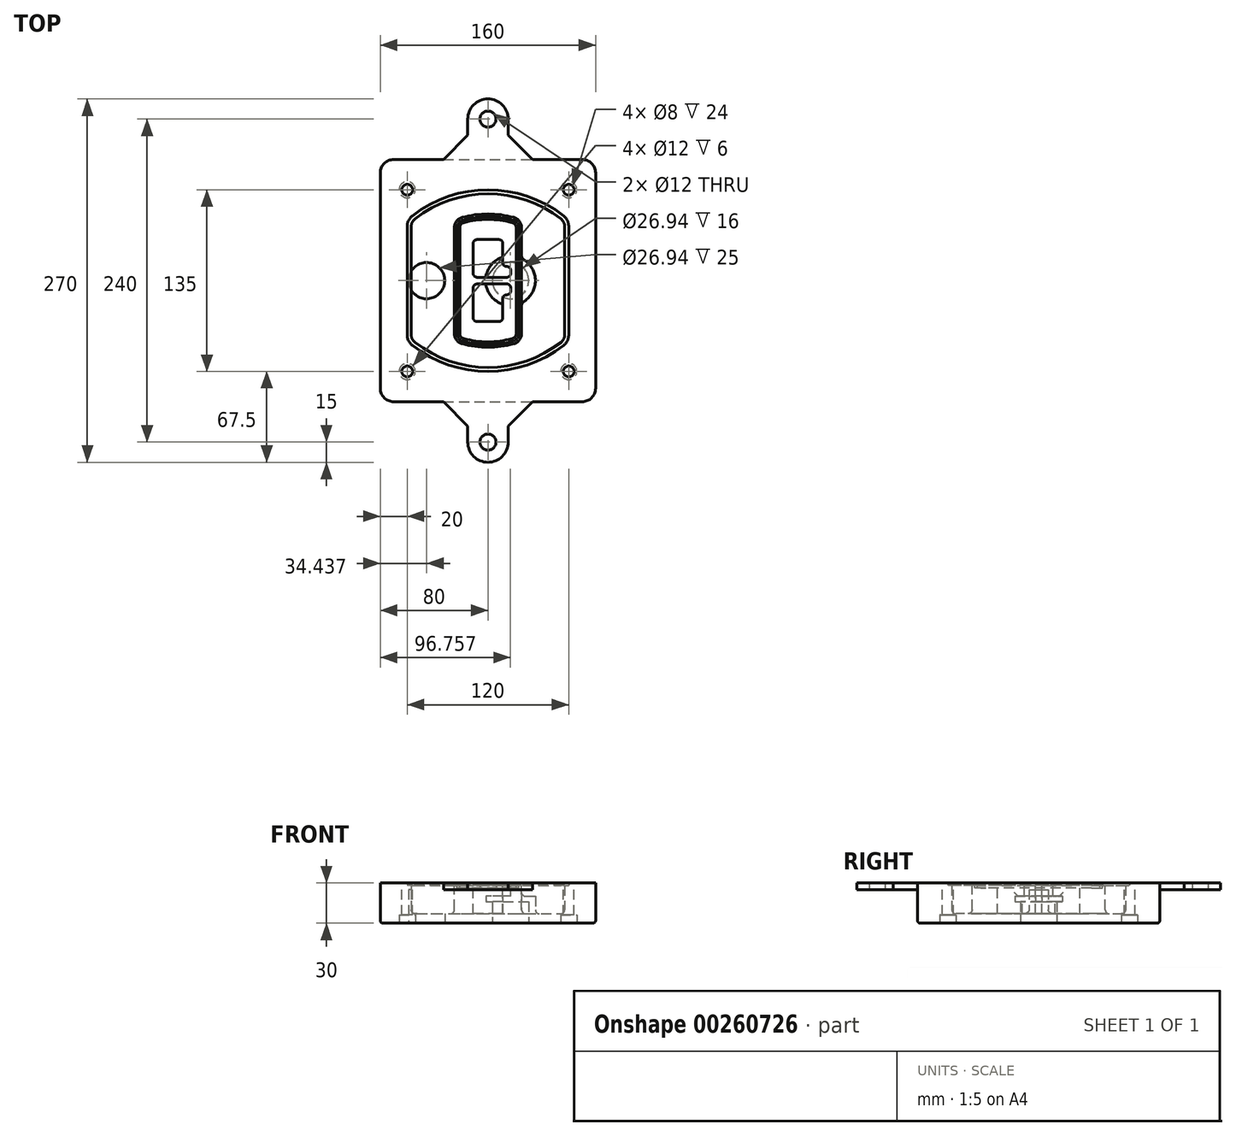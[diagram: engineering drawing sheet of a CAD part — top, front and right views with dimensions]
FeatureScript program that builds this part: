
annotation { "Feature Type Name" : "Feature", "Feature Type Description" : "" }
export const myFeature = defineFeature(function(context is Context, id is Id, definition is map)
    precondition{}
    {
        {
            var Q0;
            Q0=qCreatedBy(makeId("Top.planeOp"),FACE);
            var sketch = newSketch(context, id + "F0", { "sketchPlane" : qUnion([Q0])});
            skPoint(sketch, "E0.rect.middle", {"position": v(0, 0) * mm});
            skLineSegment(sketch, "E1.bottom", {"start": v(-70, -90) * mm, "end": v(70, -90) * mm});
            skLineSegment(sketch, "E1.top", {"start": v(-70, 90) * mm, "end": v(70, 90) * mm});
            skLineSegment(sketch, "E1.left", {"start": v(-80, -80) * mm, "end": v(-80, 80) * mm});
            skLineSegment(sketch, "E1.right", {"start": v(80, -80) * mm, "end": v(80, 80) * mm});
            skLineSegment(sketch, "E2", {"start": v(-80, 90) * mm, "end": v(80, -90) * mm, "construction": true});
            skLineSegment(sketch, "E3", {"start": v(80, 90) * mm, "end": v(-80, -90) * mm, "construction": true});
            skCircle(sketch, "E4", {"center": v(-60, 67.5) * mm, "radius": 4 * mm});
            skCircle(sketch, "E5", {"center": v(60, 67.5) * mm, "radius": 4 * mm});
            skCircle(sketch, "E6", {"center": v(60, -67.5) * mm, "radius": 4 * mm});
            skCircle(sketch, "E7", {"center": v(-60, -67.5) * mm, "radius": 4 * mm});
            skLineSegment(sketch, "E8", {"start": v(-60, 67.5) * mm, "end": v(60, 67.5) * mm, "construction": true});
            skLineSegment(sketch, "E9", {"start": v(60, 67.5) * mm, "end": v(60, -67.5) * mm, "construction": true});
            skLineSegment(sketch, "E10", {"start": v(60, -67.5) * mm, "end": v(-60, -67.5) * mm, "construction": true});
            skLineSegment(sketch, "E11", {"start": v(-60, -67.5) * mm, "end": v(-60, 67.5) * mm, "construction": true});
            skLineSegment(sketch, "E12", {"start": v(-60, 40.3) * mm, "end": v(-60, -40.3) * mm});
            skLineSegment(sketch, "E13", {"start": v(60, 40.3) * mm, "end": v(60, -40.3) * mm});
            skArc(sketch, "E14", {"start": v(56.15, 48.18) * mm, "mid": v(0, 67.5) * mm, "end": v(-56.15, 48.18) * mm});
            skArc(sketch, "E15", {"start": v(-56.15, -48.18) * mm, "mid": v(0, -67.5) * mm, "end": v(56.15, -48.18) * mm});
            skLineSegment(sketch, "E16", {"start": v(-60, 0) * mm, "end": v(60, 0) * mm, "construction": true});
            skPoint(sketch, "E17.visualSharp", {"position": v(-60, -45) * mm});
            skArc(sketch, "E17.filletArc", {"start": v(-60, -40.3) * mm, "mid": v(-58.99, -44.68) * mm, "end": v(-56.15, -48.18) * mm});
            skPoint(sketch, "E18.visualSharp", {"position": v(-60, 45) * mm});
            skArc(sketch, "E18.filletArc", {"start": v(-56.15, 48.18) * mm, "mid": v(-58.99, 44.68) * mm, "end": v(-60, 40.3) * mm});
            skPoint(sketch, "E19.visualSharp", {"position": v(60, 45) * mm});
            skArc(sketch, "E19.filletArc", {"start": v(60, 40.3) * mm, "mid": v(58.99, 44.68) * mm, "end": v(56.15, 48.18) * mm});
            skPoint(sketch, "E20.visualSharp", {"position": v(60, -45) * mm});
            skArc(sketch, "E20.filletArc", {"start": v(56.15, -48.18) * mm, "mid": v(58.99, -44.68) * mm, "end": v(60, -40.3) * mm});
            skPoint(sketch, "E21.visualSharp", {"position": v(-80, 90) * mm});
            skArc(sketch, "E21.filletArc", {"start": v(-70, 90) * mm, "mid": v(-77.07, 87.07) * mm, "end": v(-80, 80) * mm});
            skPoint(sketch, "E22.visualSharp", {"position": v(80, 90) * mm});
            skArc(sketch, "E22.filletArc", {"start": v(80, 80) * mm, "mid": v(77.07, 87.07) * mm, "end": v(70, 90) * mm});
            skPoint(sketch, "E23.visualSharp", {"position": v(80, -90) * mm});
            skArc(sketch, "E23.filletArc", {"start": v(70, -90) * mm, "mid": v(77.07, -87.07) * mm, "end": v(80, -80) * mm});
            skPoint(sketch, "E24.visualSharp", {"position": v(-80, -90) * mm});
            skArc(sketch, "E24.filletArc", {"start": v(-80, -80) * mm, "mid": v(-77.07, -87.07) * mm, "end": v(-70, -90) * mm});
            skArc(sketch, "E25.0", {"start": v(57, 40.3) * mm, "mid": v(56.3, 43.36) * mm, "end": v(54.3, 45.81) * mm});
            skLineSegment(sketch, "E25.1", {"start": v(57, 40.3) * mm, "end": v(57, -40.3) * mm});
            skArc(sketch, "E25.2", {"start": v(54.3, -45.81) * mm, "mid": v(56.3, -43.36) * mm, "end": v(57, -40.3) * mm});
            skArc(sketch, "E25.3", {"start": v(-54.3, -45.81) * mm, "mid": v(0, -64.5) * mm, "end": v(54.3, -45.81) * mm});
            skArc(sketch, "E25.4", {"start": v(-57, -40.3) * mm, "mid": v(-56.3, -43.36) * mm, "end": v(-54.3, -45.81) * mm});
            skArc(sketch, "E25.5", {"start": v(54.3, 45.81) * mm, "mid": v(0, 64.5) * mm, "end": v(-54.3, 45.81) * mm});
            skLineSegment(sketch, "E25.6", {"start": v(-57, 40.3) * mm, "end": v(-57, -40.3) * mm});
            skArc(sketch, "E25.7", {"start": v(-54.3, 45.81) * mm, "mid": v(-56.3, 43.36) * mm, "end": v(-57, 40.3) * mm});
            skArc(sketch, "E26.0", {"start": v(-58.62, 51.33) * mm, "mid": v(-62.58, 46.43) * mm, "end": v(-64, 40.3) * mm});
            skArc(sketch, "E26.1", {"start": v(58.62, 51.33) * mm, "mid": v(0, 71.5) * mm, "end": v(-58.62, 51.33) * mm});
            skArc(sketch, "E26.2", {"start": v(64, 40.3) * mm, "mid": v(62.58, 46.43) * mm, "end": v(58.62, 51.33) * mm});
            skLineSegment(sketch, "E26.3", {"start": v(64, 40.3) * mm, "end": v(64, -40.3) * mm});
            skArc(sketch, "E26.4", {"start": v(58.62, -51.33) * mm, "mid": v(62.58, -46.43) * mm, "end": v(64, -40.3) * mm});
            skLineSegment(sketch, "E26.5", {"start": v(-64, 40.3) * mm, "end": v(-64, -40.3) * mm});
            skArc(sketch, "E26.6", {"start": v(-58.62, -51.33) * mm, "mid": v(0, -71.5) * mm, "end": v(58.62, -51.33) * mm});
            skArc(sketch, "E26.7", {"start": v(-64, -40.3) * mm, "mid": v(-62.58, -46.43) * mm, "end": v(-58.62, -51.33) * mm});
            skSolve(sketch);
        }
        {
            var Q0;
            Q0=makeQuery(id+"F0.imprint","IMPRINT",FACE,{"disambiguationData":[TD([[makeQuery(id+"F0.imprint","IMPRINT",EDGE,{"derivedFrom":sQuery(id+"F0.wireOp",EDGE,"E1.bottom")}),1.0]])]});
            var Q1;
            Q1=makeQuery(id+"F0.imprint","IMPRINT",FACE,{"disambiguationData":[TD([[makeQuery(id+"F0.imprint","IMPRINT",EDGE,{"derivedFrom":sQuery(id+"F0.wireOp",EDGE,"E12")}),1.0]])]});
            var Q2;
            Q2=makeQuery(id+"F0.imprint","IMPRINT",FACE,{"disambiguationData":[TD([[makeQuery(id+"F0.imprint","IMPRINT",EDGE,{"derivedFrom":sQuery(id+"F0.wireOp",EDGE,"E25.0")}),1.0]])]});
            var Q3;
            Q3=makeQuery(id+"F0.imprint","IMPRINT",FACE,{"disambiguationData":[TD([[makeQuery(id+"F0.imprint","IMPRINT",EDGE,{"derivedFrom":sQuery(id+"F0.wireOp",EDGE,"E12")}),-1.0]])]});
            extrude(context, id + "F1", {"entities" : qUnion([Q0, Q1, Q2, Q3]), "oppositeDirection" : true, "depth" : 25 * mm});
        }
        {
            var Q0;
            Q0=makeQuery(id+"F0.imprint","IMPRINT",FACE,{"disambiguationData":[TD([[makeQuery(id+"F0.imprint","IMPRINT",EDGE,{"derivedFrom":sQuery(id+"F0.wireOp",EDGE,"E12")}),1.0]])]});
            extrude(context, id + "F2", {"entities" : qUnion([Q0]), "operationType" : NewBodyOperationType.ADD, "depth" : 3 * mm});
        }
        {
            var Q0;
            Q0=makeQuery(id+"F0.imprint","IMPRINT",FACE,{"disambiguationData":[TD([[makeQuery(id+"F0.imprint","IMPRINT",EDGE,{"derivedFrom":sQuery(id+"F0.wireOp",EDGE,"E25.0")}),1.0]])]});
            extrude(context, id + "F3", {"entities" : qUnion([Q0]), "operationType" : NewBodyOperationType.REMOVE, "oppositeDirection" : true, "depth" : 18 * mm});
        }
        {
            var Q0;
            Q0=makeQuery(id+"F2.opExtrude","CAP_FACE",FACE,{"disambiguationData":[OSD([sQuery(id+"F0.wireOp",EDGE,"E12"),sQuery(id+"F0.wireOp",EDGE,"E13"),sQuery(id+"F0.wireOp",EDGE,"E14"),sQuery(id+"F0.wireOp",EDGE,"E15"),sQuery(id+"F0.wireOp",EDGE,"E17.filletArc"),sQuery(id+"F0.wireOp",EDGE,"E18.filletArc"),sQuery(id+"F0.wireOp",EDGE,"E19.filletArc"),sQuery(id+"F0.wireOp",EDGE,"E20.filletArc"),sQuery(id+"F0.wireOp",EDGE,"E25.0"),sQuery(id+"F0.wireOp",EDGE,"E25.1"),sQuery(id+"F0.wireOp",EDGE,"E25.2"),sQuery(id+"F0.wireOp",EDGE,"E25.3"),sQuery(id+"F0.wireOp",EDGE,"E25.4"),sQuery(id+"F0.wireOp",EDGE,"E25.5"),sQuery(id+"F0.wireOp",EDGE,"E25.6"),sQuery(id+"F0.wireOp",EDGE,"E25.7")])],"isStart":false});
            var sketch = newSketch(context, id + "F4", { "sketchPlane" : qUnion([Q0])});
            skArc(sketch, "E27.0", {"start": v(-19.08, -46.97) * mm, "mid": v(0, -49.5) * mm, "end": v(19.08, -46.97) * mm});
            skArc(sketch, "E28.0", {"start": v(19.08, 46.97) * mm, "mid": v(0, 49.5) * mm, "end": v(-19.08, 46.97) * mm});
            skLineSegment(sketch, "E29", {"start": v(-25, 39.25) * mm, "end": v(-25, -39.25) * mm});
            skLineSegment(sketch, "E30", {"start": v(25, 39.25) * mm, "end": v(25, -39.25) * mm});
            skLineSegment(sketch, "E31", {"start": v(-25, 45.1) * mm, "end": v(25, 45.1) * mm, "construction": true});
            skLineSegment(sketch, "E32", {"start": v(-25, -45.1) * mm, "end": v(25, -45.1) * mm, "construction": true});
            skPoint(sketch, "E33.visualSharp", {"position": v(-25, 45.1) * mm});
            skArc(sketch, "E33.filletArc", {"start": v(-19.08, 46.97) * mm, "mid": v(-23.35, 44.11) * mm, "end": v(-25, 39.25) * mm});
            skPoint(sketch, "E34.visualSharp", {"position": v(25, 45.1) * mm});
            skArc(sketch, "E34.filletArc", {"start": v(25, 39.25) * mm, "mid": v(23.35, 44.11) * mm, "end": v(19.08, 46.97) * mm});
            skPoint(sketch, "E35.visualSharp", {"position": v(25, -45.1) * mm});
            skArc(sketch, "E35.filletArc", {"start": v(19.08, -46.97) * mm, "mid": v(23.35, -44.11) * mm, "end": v(25, -39.25) * mm});
            skPoint(sketch, "E36.visualSharp", {"position": v(-25, -45.1) * mm});
            skArc(sketch, "E36.filletArc", {"start": v(-25, -39.25) * mm, "mid": v(-23.35, -44.11) * mm, "end": v(-19.08, -46.97) * mm});
            skArc(sketch, "E37.0", {"start": v(54.3, 45.81) * mm, "mid": v(0, 64.5) * mm, "end": v(-54.3, 45.81) * mm});
            skArc(sketch, "E37.1", {"start": v(-54.3, 45.81) * mm, "mid": v(-56.3, 43.36) * mm, "end": v(-57, 40.3) * mm});
            skLineSegment(sketch, "E37.2", {"start": v(-57, 40.3) * mm, "end": v(-57, -40.3) * mm});
            skArc(sketch, "E37.3", {"start": v(-57, -40.3) * mm, "mid": v(-56.3, -43.36) * mm, "end": v(-54.3, -45.81) * mm});
            skArc(sketch, "E37.4", {"start": v(-54.3, -45.81) * mm, "mid": v(0, -64.5) * mm, "end": v(54.3, -45.81) * mm});
            skArc(sketch, "E37.5", {"start": v(54.3, -45.81) * mm, "mid": v(56.3, -43.36) * mm, "end": v(57, -40.3) * mm});
            skLineSegment(sketch, "E37.6", {"start": v(57, 40.3) * mm, "end": v(57, -40.3) * mm});
            skArc(sketch, "E37.7", {"start": v(57, 40.3) * mm, "mid": v(56.3, 43.36) * mm, "end": v(54.3, 45.81) * mm});
            skLineSegment(sketch, "E38.0", {"start": v(23, 39.25) * mm, "end": v(23, -39.25) * mm});
            skArc(sketch, "E38.1", {"start": v(18.56, -45.04) * mm, "mid": v(21.76, -42.9) * mm, "end": v(23, -39.25) * mm});
            skArc(sketch, "E38.2", {"start": v(-18.56, -45.04) * mm, "mid": v(0, -47.5) * mm, "end": v(18.56, -45.04) * mm});
            skArc(sketch, "E38.3", {"start": v(-23, -39.25) * mm, "mid": v(-21.76, -42.9) * mm, "end": v(-18.56, -45.04) * mm});
            skLineSegment(sketch, "E38.4", {"start": v(-23, 39.25) * mm, "end": v(-23, -39.25) * mm});
            skArc(sketch, "E38.5", {"start": v(23, 39.25) * mm, "mid": v(21.76, 42.9) * mm, "end": v(18.56, 45.04) * mm});
            skArc(sketch, "E38.6", {"start": v(-18.56, 45.04) * mm, "mid": v(-21.76, 42.9) * mm, "end": v(-23, 39.25) * mm});
            skArc(sketch, "E38.7", {"start": v(18.56, 45.04) * mm, "mid": v(0, 47.5) * mm, "end": v(-18.56, 45.04) * mm});
            skArc(sketch, "E39.0", {"start": v(21, 39.25) * mm, "mid": v(20.18, 41.68) * mm, "end": v(18.04, 43.1) * mm});
            skLineSegment(sketch, "E39.1", {"start": v(21, 39.25) * mm, "end": v(21, -39.25) * mm});
            skArc(sketch, "E39.2", {"start": v(18.04, -43.1) * mm, "mid": v(20.18, -41.68) * mm, "end": v(21, -39.25) * mm});
            skArc(sketch, "E39.3", {"start": v(-18.04, -43.1) * mm, "mid": v(0, -45.5) * mm, "end": v(18.04, -43.1) * mm});
            skArc(sketch, "E39.4", {"start": v(-21, -39.25) * mm, "mid": v(-20.18, -41.68) * mm, "end": v(-18.04, -43.1) * mm});
            skArc(sketch, "E39.5", {"start": v(18.04, 43.1) * mm, "mid": v(0, 45.5) * mm, "end": v(-18.04, 43.1) * mm});
            skLineSegment(sketch, "E39.6", {"start": v(-21, 39.25) * mm, "end": v(-21, -39.25) * mm});
            skArc(sketch, "E39.7", {"start": v(-18.04, 43.1) * mm, "mid": v(-20.18, 41.68) * mm, "end": v(-21, 39.25) * mm});
            skLineSegment(sketch, "E40", {"start": v(-25, 0) * mm, "end": v(25, 0) * mm, "construction": true});
            skLineSegment(sketch, "E41", {"start": v(-11, 5.5) * mm, "end": v(-11, 27.5) * mm});
            skLineSegment(sketch, "E42", {"start": v(-8, 30.5) * mm, "end": v(8, 30.5) * mm});
            skLineSegment(sketch, "E43", {"start": v(11, 27.5) * mm, "end": v(11, 13.5) * mm});
            skLineSegment(sketch, "E44", {"start": v(14, 10.5) * mm, "end": v(14, 10.5) * mm});
            skLineSegment(sketch, "E45", {"start": v(17, 7.5) * mm, "end": v(17, 5.5) * mm});
            skLineSegment(sketch, "E46", {"start": v(14, 2.5) * mm, "end": v(-8, 2.5) * mm});
            skPoint(sketch, "E47.visualSharp", {"position": v(-11, 30.5) * mm});
            skArc(sketch, "E47.filletArc", {"start": v(-8, 30.5) * mm, "mid": v(-10.12, 29.62) * mm, "end": v(-11, 27.5) * mm});
            skPoint(sketch, "E48.visualSharp", {"position": v(11, 30.5) * mm});
            skArc(sketch, "E48.filletArc", {"start": v(11, 27.5) * mm, "mid": v(10.12, 29.62) * mm, "end": v(8, 30.5) * mm});
            skPoint(sketch, "E49.visualSharp", {"position": v(11, 10.5) * mm});
            skArc(sketch, "E49.filletArc", {"start": v(11, 13.5) * mm, "mid": v(11.88, 11.38) * mm, "end": v(14, 10.5) * mm});
            skPoint(sketch, "E50.visualSharp", {"position": v(17, 10.5) * mm});
            skArc(sketch, "E50.filletArc", {"start": v(17, 7.5) * mm, "mid": v(16.12, 9.62) * mm, "end": v(14, 10.5) * mm});
            skPoint(sketch, "E51.visualSharp", {"position": v(17, 2.5) * mm});
            skArc(sketch, "E51.filletArc", {"start": v(14, 2.5) * mm, "mid": v(16.12, 3.38) * mm, "end": v(17, 5.5) * mm});
            skPoint(sketch, "E52.visualSharp", {"position": v(-11, 2.5) * mm});
            skArc(sketch, "E52.filletArc", {"start": v(-11, 5.5) * mm, "mid": v(-10.12, 3.38) * mm, "end": v(-8, 2.5) * mm});
            skLineSegment(sketch, "E53.0.MirrorCS", {"start": v(14, -2.5) * mm, "end": v(-8, -2.5) * mm});
            skArc(sketch, "E54.0.MirrorCS", {"start": v(-11, -5.5) * mm, "mid": v(-10.12, -3.38) * mm, "end": v(-8, -2.5) * mm});
            skLineSegment(sketch, "E55.0.MirrorCS", {"start": v(-11, -5.5) * mm, "end": v(-11, -27.5) * mm});
            skArc(sketch, "E56.0.MirrorCS", {"start": v(-8, -30.5) * mm, "mid": v(-10.12, -29.62) * mm, "end": v(-11, -27.5) * mm});
            skLineSegment(sketch, "E57.0.MirrorCS", {"start": v(-8, -30.5) * mm, "end": v(8, -30.5) * mm});
            skArc(sketch, "E58.0.MirrorCS", {"start": v(11, -27.5) * mm, "mid": v(10.12, -29.62) * mm, "end": v(8, -30.5) * mm});
            skLineSegment(sketch, "E59.0.MirrorCS", {"start": v(11, -27.5) * mm, "end": v(11, -13.5) * mm});
            skArc(sketch, "E60.0.MirrorCS", {"start": v(11, -13.5) * mm, "mid": v(11.88, -11.38) * mm, "end": v(14, -10.5) * mm});
            skArc(sketch, "E61.0.MirrorCS", {"start": v(17, -7.5) * mm, "mid": v(16.12, -9.62) * mm, "end": v(14, -10.5) * mm});
            skLineSegment(sketch, "E62.0.MirrorCS", {"start": v(17, -7.5) * mm, "end": v(17, -5.5) * mm});
            skArc(sketch, "E63.0.MirrorCS", {"start": v(14, -2.5) * mm, "mid": v(16.12, -3.38) * mm, "end": v(17, -5.5) * mm});
            skSolve(sketch);
        }
        {
            var Q0;
            Q0=makeQuery(id+"F4.imprint","IMPRINT",FACE,{"disambiguationData":[TD([[makeQuery(id+"F4.imprint","IMPRINT",EDGE,{"derivedFrom":sQuery(id+"F4.wireOp",EDGE,"E27.0")}),1.0]])]});
            var Q1;
            Q1=makeQuery(id+"F4.imprint","IMPRINT",FACE,{"disambiguationData":[TD([[makeQuery(id+"F4.imprint","IMPRINT",EDGE,{"derivedFrom":sQuery(id+"F4.wireOp",EDGE,"E38.0")}),-1.0]])]});
            var Q2;
            Q2=makeQuery(id+"F4.imprint","IMPRINT",FACE,{"disambiguationData":[TD([[makeQuery(id+"F4.imprint","IMPRINT",EDGE,{"derivedFrom":sQuery(id+"F4.wireOp",EDGE,"E39.0")}),1.0]])]});
            extrude(context, id + "F5", {"entities" : qUnion([Q0, Q1, Q2]), "operationType" : NewBodyOperationType.ADD, "endBound" : BoundingType.UP_TO_NEXT, "oppositeDirection" : true, "depth" : 25 * mm});
        }
        {
            var Q0;
            Q0=makeQuery(id+"F4.imprint","IMPRINT",FACE,{"disambiguationData":[TD([[makeQuery(id+"F4.imprint","IMPRINT",EDGE,{"derivedFrom":sQuery(id+"F4.wireOp",EDGE,"E38.0")}),-1.0]])]});
            extrude(context, id + "F6", {"entities" : qUnion([Q0]), "operationType" : NewBodyOperationType.REMOVE, "oppositeDirection" : true, "depth" : 2 * mm});
        }
        {
            var Q0;
            Q0=makeQuery(id+"F1.opExtrude","CAP_FACE",FACE,{"disambiguationData":[OSD([sQuery(id+"F0.wireOp",EDGE,"E1.bottom"),sQuery(id+"F0.wireOp",EDGE,"E1.top"),sQuery(id+"F0.wireOp",EDGE,"E1.left"),sQuery(id+"F0.wireOp",EDGE,"E1.right"),sQuery(id+"F0.wireOp",EDGE,"E4"),sQuery(id+"F0.wireOp",EDGE,"E5"),sQuery(id+"F0.wireOp",EDGE,"E6"),sQuery(id+"F0.wireOp",EDGE,"E7"),sQuery(id+"F0.wireOp",EDGE,"E21.filletArc"),sQuery(id+"F0.wireOp",EDGE,"E22.filletArc"),sQuery(id+"F0.wireOp",EDGE,"E23.filletArc"),sQuery(id+"F0.wireOp",EDGE,"E24.filletArc")])],"isStart":false});
            var sketch = newSketch(context, id + "F7", { "sketchPlane" : qUnion([Q0])});
            skCircle(sketch, "E64", {"center": v(16.76, 0) * mm, "radius": 13.47 * mm});
            skCircle(sketch, "E65", {"center": v(-45.56, 0) * mm, "radius": 13.47 * mm});
            skLineSegment(sketch, "E66", {"start": v(80, 0) * mm, "end": v(-80, 0) * mm});
            skCircle(sketch, "E67", {"center": v(16.76, 0) * mm, "radius": 18.47 * mm});
            skCircle(sketch, "E68", {"center": v(60, -67.5) * mm, "radius": 6 * mm});
            skCircle(sketch, "E69", {"center": v(-60, -67.5) * mm, "radius": 6 * mm});
            skCircle(sketch, "E70", {"center": v(-60, 67.5) * mm, "radius": 6 * mm});
            skCircle(sketch, "E71", {"center": v(60, 67.5) * mm, "radius": 6 * mm});
            skSolve(sketch);
        }
        {
            var Q0;
            {var subQ1=sQuery(id+"F7.wireOp",EDGE,"E66");var subQ4=sQuery(id+"F7.wireOp",EDGE,"E64");var subQ6=makeQuery(id+"F7.imprint","INTERSECT",VERTEX,{"disambiguationData":[OD(0.0)],"derivedFrom":[subQ4,subQ1]});Q0=makeQuery(id+"F7.imprint","IMPRINT",FACE,{"disambiguationData":[TD([[makeQuery(id+"F7.imprint","IMPRINT",EDGE,{"disambiguationData":[TD([[subQ6,-1.0]])],"derivedFrom":subQ4}),-1.0]])]});}
            var Q1;
            {var subQ0=sQuery(id+"F7.wireOp",EDGE,"E66");var subQ1=sQuery(id+"F7.wireOp",EDGE,"E64");var subQ3=makeQuery(id+"F7.imprint","INTERSECT",VERTEX,{"disambiguationData":[OD(0.0)],"derivedFrom":[subQ1,subQ0]});Q1=makeQuery(id+"F7.imprint","IMPRINT",FACE,{"disambiguationData":[TD([[makeQuery(id+"F7.imprint","IMPRINT",EDGE,{"disambiguationData":[TD([[subQ3,-1.0]])],"derivedFrom":subQ1}),1.0]])]});}
            var Q2;
            {var subQ0=sQuery(id+"F7.wireOp",EDGE,"E66");var subQ1=sQuery(id+"F7.wireOp",EDGE,"E64");var subQ3=makeQuery(id+"F7.imprint","INTERSECT",VERTEX,{"disambiguationData":[OD(0.0)],"derivedFrom":[subQ1,subQ0]});Q2=makeQuery(id+"F7.imprint","IMPRINT",FACE,{"disambiguationData":[TD([[makeQuery(id+"F7.imprint","IMPRINT",EDGE,{"disambiguationData":[TD([[subQ3,1.0]])],"derivedFrom":subQ1}),1.0]])]});}
            var Q3;
            {var subQ1=sQuery(id+"F7.wireOp",EDGE,"E66");var subQ4=sQuery(id+"F7.wireOp",EDGE,"E64");var subQ6=makeQuery(id+"F7.imprint","INTERSECT",VERTEX,{"disambiguationData":[OD(0.0)],"derivedFrom":[subQ4,subQ1]});Q3=makeQuery(id+"F7.imprint","IMPRINT",FACE,{"disambiguationData":[TD([[makeQuery(id+"F7.imprint","IMPRINT",EDGE,{"disambiguationData":[TD([[subQ6,1.0]])],"derivedFrom":subQ4}),-1.0]])]});}
            extrude(context, id + "F8", {"entities" : qUnion([Q0, Q1, Q2, Q3]), "operationType" : NewBodyOperationType.ADD, "oppositeDirection" : true, "depth" : 20 * mm});
        }
        {
            var Q0;
            {var subQ0=sQuery(id+"F7.wireOp",EDGE,"E66");var subQ1=sQuery(id+"F7.wireOp",EDGE,"E64");var subQ3=makeQuery(id+"F7.imprint","INTERSECT",VERTEX,{"disambiguationData":[OD(0.0)],"derivedFrom":[subQ1,subQ0]});Q0=makeQuery(id+"F7.imprint","IMPRINT",FACE,{"disambiguationData":[TD([[makeQuery(id+"F7.imprint","IMPRINT",EDGE,{"disambiguationData":[TD([[subQ3,-1.0]])],"derivedFrom":subQ1}),1.0]])]});}
            var Q1;
            {var subQ0=sQuery(id+"F7.wireOp",EDGE,"E66");var subQ1=sQuery(id+"F7.wireOp",EDGE,"E64");var subQ3=makeQuery(id+"F7.imprint","INTERSECT",VERTEX,{"disambiguationData":[OD(0.0)],"derivedFrom":[subQ1,subQ0]});Q1=makeQuery(id+"F7.imprint","IMPRINT",FACE,{"disambiguationData":[TD([[makeQuery(id+"F7.imprint","IMPRINT",EDGE,{"disambiguationData":[TD([[subQ3,1.0]])],"derivedFrom":subQ1}),1.0]])]});}
            extrude(context, id + "F9", {"entities" : qUnion([Q0, Q1]), "operationType" : NewBodyOperationType.REMOVE, "oppositeDirection" : true, "depth" : 16 * mm});
        }
        {
            var Q0;
            {var subQ0=sQuery(id+"F7.wireOp",EDGE,"E66");var subQ1=sQuery(id+"F7.wireOp",EDGE,"E65");var subQ3=makeQuery(id+"F7.imprint","INTERSECT",VERTEX,{"disambiguationData":[OD(0.0)],"derivedFrom":[subQ1,subQ0]});Q0=makeQuery(id+"F7.imprint","IMPRINT",FACE,{"disambiguationData":[TD([[makeQuery(id+"F7.imprint","IMPRINT",EDGE,{"disambiguationData":[TD([[subQ3,-1.0]])],"derivedFrom":subQ1}),1.0]])]});}
            var Q1;
            {var subQ0=sQuery(id+"F7.wireOp",EDGE,"E66");var subQ1=sQuery(id+"F7.wireOp",EDGE,"E65");var subQ3=makeQuery(id+"F7.imprint","INTERSECT",VERTEX,{"disambiguationData":[OD(0.0)],"derivedFrom":[subQ1,subQ0]});Q1=makeQuery(id+"F7.imprint","IMPRINT",FACE,{"disambiguationData":[TD([[makeQuery(id+"F7.imprint","IMPRINT",EDGE,{"disambiguationData":[TD([[subQ3,1.0]])],"derivedFrom":subQ1}),1.0]])]});}
            extrude(context, id + "F10", {"entities" : qUnion([Q0, Q1]), "operationType" : NewBodyOperationType.REMOVE, "oppositeDirection" : true, "depth" : 25 * mm});
        }
        {
            var Q0;
            Q0=makeQuery(id+"F7.imprint","IMPRINT",FACE,{"disambiguationData":[TD([[makeQuery(id+"F7.imprint","IMPRINT",EDGE,{"derivedFrom":sQuery(id+"F7.wireOp",EDGE,"E68")}),1.0]])]});
            var Q1;
            Q1=makeQuery(id+"F7.imprint","IMPRINT",FACE,{"disambiguationData":[TD([[makeQuery(id+"F7.imprint","IMPRINT",EDGE,{"derivedFrom":makeQuery(id+"F1.opExtrude","CAP_EDGE",EDGE,{"disambiguationData":[OSD([sQuery(id+"F0.wireOp",EDGE,"E5")])],"isStart":false})}),-1.0]])]});
            var Q2;
            Q2=makeQuery(id+"F7.imprint","IMPRINT",FACE,{"disambiguationData":[TD([[makeQuery(id+"F7.imprint","IMPRINT",EDGE,{"derivedFrom":sQuery(id+"F7.wireOp",EDGE,"E69")}),1.0]])]});
            var Q3;
            Q3=makeQuery(id+"F7.imprint","IMPRINT",FACE,{"disambiguationData":[TD([[makeQuery(id+"F7.imprint","IMPRINT",EDGE,{"derivedFrom":makeQuery(id+"F1.opExtrude","CAP_EDGE",EDGE,{"disambiguationData":[OSD([sQuery(id+"F0.wireOp",EDGE,"E4")])],"isStart":false})}),-1.0]])]});
            var Q4;
            Q4=makeQuery(id+"F7.imprint","IMPRINT",FACE,{"disambiguationData":[TD([[makeQuery(id+"F7.imprint","IMPRINT",EDGE,{"derivedFrom":sQuery(id+"F7.wireOp",EDGE,"E70")}),1.0]])]});
            var Q5;
            Q5=makeQuery(id+"F7.imprint","IMPRINT",FACE,{"disambiguationData":[TD([[makeQuery(id+"F7.imprint","IMPRINT",EDGE,{"derivedFrom":makeQuery(id+"F1.opExtrude","CAP_EDGE",EDGE,{"disambiguationData":[OSD([sQuery(id+"F0.wireOp",EDGE,"E7")])],"isStart":false})}),-1.0]])]});
            var Q6;
            Q6=makeQuery(id+"F7.imprint","IMPRINT",FACE,{"disambiguationData":[TD([[makeQuery(id+"F7.imprint","IMPRINT",EDGE,{"derivedFrom":sQuery(id+"F7.wireOp",EDGE,"E71")}),1.0]])]});
            var Q7;
            Q7=makeQuery(id+"F7.imprint","IMPRINT",FACE,{"disambiguationData":[TD([[makeQuery(id+"F7.imprint","IMPRINT",EDGE,{"derivedFrom":makeQuery(id+"F1.opExtrude","CAP_EDGE",EDGE,{"disambiguationData":[OSD([sQuery(id+"F0.wireOp",EDGE,"E6")])],"isStart":false})}),-1.0]])]});
            extrude(context, id + "F11", {"entities" : qUnion([Q0, Q1, Q2, Q3, Q4, Q5, Q6, Q7]), "operationType" : NewBodyOperationType.REMOVE, "oppositeDirection" : true, "depth" : 6 * mm});
        }
        {
            var Q0;
            Q0=makeQuery(id+"F9.boolean.opBoolean","COPY",FACE,{"derivedFrom":makeQuery(id+"F9.opExtrude","CAP_FACE",FACE,{"disambiguationData":[OSD([sQuery(id+"F7.wireOp",EDGE,"E64")])],"isStart":false})});
            var sketch = newSketch(context, id + "F12", { "sketchPlane" : qUnion([Q0])});
            skArc(sketch, "E72.0", {"start": v(11, 17.55) * mm, "mid": v(2.57, 11.82) * mm, "end": v(-1.54, 2.5) * mm});
            skArc(sketch, "E72.1", {"start": v(-1.54, -2.5) * mm, "mid": v(2.57, -11.82) * mm, "end": v(11, -17.55) * mm});
            skLineSegment(sketch, "E73", {"start": v(-1.54, -2.5) * mm, "end": v(14, -2.5) * mm});
            skLineSegment(sketch, "E74.0", {"start": v(14, 2.5) * mm, "end": v(-1.54, 2.5) * mm});
            skArc(sketch, "E74.1", {"start": v(14, 2.5) * mm, "mid": v(16.12, 3.38) * mm, "end": v(17, 5.5) * mm});
            skLineSegment(sketch, "E74.2", {"start": v(17, 7.5) * mm, "end": v(17, 5.5) * mm});
            skArc(sketch, "E74.3", {"start": v(17, 7.5) * mm, "mid": v(16.12, 9.62) * mm, "end": v(14, 10.5) * mm});
            skArc(sketch, "E74.4", {"start": v(11, 13.5) * mm, "mid": v(11.88, 11.38) * mm, "end": v(14, 10.5) * mm});
            skLineSegment(sketch, "E74.5", {"start": v(11, 17.55) * mm, "end": v(11, 13.5) * mm});
            skLineSegment(sketch, "E74.7", {"start": v(14, -2.5) * mm, "end": v(-1.54, -2.5) * mm});
            skArc(sketch, "E74.8", {"start": v(14, -2.5) * mm, "mid": v(16.12, -3.38) * mm, "end": v(17, -5.5) * mm});
            skLineSegment(sketch, "E74.9", {"start": v(17, -7.5) * mm, "end": v(17, -5.5) * mm});
            skArc(sketch, "E74.10", {"start": v(17, -7.5) * mm, "mid": v(16.12, -9.62) * mm, "end": v(14, -10.5) * mm});
            skArc(sketch, "E74.11", {"start": v(11, -13.5) * mm, "mid": v(11.88, -11.38) * mm, "end": v(14, -10.5) * mm});
            skLineSegment(sketch, "E74.12", {"start": v(11, -17.55) * mm, "end": v(11, -13.5) * mm});
            skPoint(sketch, "E75.orphan", {"position": v(11, -27.5) * mm});
            skPoint(sketch, "E76.orphan", {"position": v(-8, -2.5) * mm});
            skPoint(sketch, "E77.orphan", {"position": v(-8, 2.5) * mm});
            skPoint(sketch, "E78.orphan", {"position": v(11, 27.5) * mm});
            skSolve(sketch);
        }
        {
            var Q0;
            {var subQ7=sQuery(id+"F12.wireOp",EDGE,"E72.0");var subQ14=sQuery(id+"F12.wireOp",EDGE,"E72.1");var subQ16=sQuery(id+"F12.wireOp",EDGE,"E74.1");var subQ18=sQuery(id+"F12.wireOp",EDGE,"E74.8");Q0=qUnion([makeQuery(id+"F12.imprint","IMPRINT",FACE,{"disambiguationData":[TD([[makeQuery(id+"F12.imprint","IMPRINT",EDGE,{"derivedFrom":subQ7}),1.0]])]}),makeQuery(id+"F12.imprint","IMPRINT",FACE,{"disambiguationData":[TD([[makeQuery(id+"F12.imprint","IMPRINT",EDGE,{"derivedFrom":subQ14}),1.0]])]}),makeQuery(id+"F12.imprint","IMPRINT",FACE,{"disambiguationData":[TD([[makeQuery(id+"F12.imprint","IMPRINT",EDGE,{"derivedFrom":subQ16}),1.0]])]}),makeQuery(id+"F12.imprint","IMPRINT",FACE,{"disambiguationData":[TD([[makeQuery(id+"F12.imprint","IMPRINT",EDGE,{"derivedFrom":subQ18}),-1.0]])]})]);}
            var Q1;
            Q1=makeQuery(id+"F5.boolean.opBoolean","SPLIT",FACE,{"disambiguationData":[TD([makeQuery(id+"F5.opExtrude","SWEPT_FACE",FACE,{"disambiguationData":[OSD([sQuery(id+"F4.wireOp",EDGE,"E41")])]})])],"derivedFrom":makeQuery(id+"F3.boolean.opBoolean","COPY",FACE,{"derivedFrom":makeQuery(id+"F3.opExtrude","CAP_FACE",FACE,{"disambiguationData":[OSD([sQuery(id+"F0.wireOp",EDGE,"E25.0"),sQuery(id+"F0.wireOp",EDGE,"E25.1"),sQuery(id+"F0.wireOp",EDGE,"E25.2"),sQuery(id+"F0.wireOp",EDGE,"E25.3"),sQuery(id+"F0.wireOp",EDGE,"E25.4"),sQuery(id+"F0.wireOp",EDGE,"E25.5"),sQuery(id+"F0.wireOp",EDGE,"E25.6"),sQuery(id+"F0.wireOp",EDGE,"E25.7")])],"isStart":false})})});
            extrude(context, id + "F13", {"entities" : qUnion([Q0]), "operationType" : NewBodyOperationType.REMOVE, "endBound" : BoundingType.UP_TO_SURFACE, "endBoundEntityFace" : qUnion([Q1]), "depth" : 25 * mm});
        }
        {
            var Q0;
            Q0=makeQuery(id+"F3.boolean.opBoolean","COPY",EDGE,{"derivedFrom":makeQuery(id+"F3.opExtrude","CAP_EDGE",EDGE,{"disambiguationData":[OSD([sQuery(id+"F0.wireOp",EDGE,"E25.6")])],"isStart":false})});
            var Q1;
            Q1=makeQuery(id+"F8.boolean.opBoolean","INTERSECT",EDGE,{"derivedFrom":[makeQuery(id+"F5.opExtrude","SWEPT_FACE",FACE,{"disambiguationData":[OSD([sQuery(id+"F4.wireOp",EDGE,"E30")])]}),makeQuery(id+"F8.opExtrude","CAP_FACE",FACE,{"disambiguationData":[OSD([sQuery(id+"F7.wireOp",EDGE,"E67")])],"isStart":false})]});
            var Q2;
            Q2=makeQuery(id+"F8.boolean.opBoolean","INTERSECT",EDGE,{"disambiguationData":[OD(1.0)],"derivedFrom":[makeQuery(id+"F5.opExtrude","SWEPT_FACE",FACE,{"disambiguationData":[OSD([sQuery(id+"F4.wireOp",EDGE,"E30")])]}),makeQuery(id+"F8.opExtrude","SWEPT_FACE",FACE,{"disambiguationData":[OSD([sQuery(id+"F7.wireOp",EDGE,"E67")])]})]});
            var Q3;
            {var subQ0=sQuery(id+"F4.wireOp",EDGE,"E30");Q3=makeQuery(id+"F8.boolean.opBoolean","SPLIT",EDGE,{"disambiguationData":[TD([makeQuery(id+"F5.opExtrude","SWEPT_FACE",FACE,{"disambiguationData":[OSD([sQuery(id+"F4.wireOp",EDGE,"E35.filletArc")])]})])],"derivedFrom":makeQuery(id+"F5.opExtrude","CAP_EDGE",EDGE,{"disambiguationData":[OSD([subQ0])],"isStart":false})});}
            var Q4;
            {var subQ0=sQuery(id+"F0.wireOp",EDGE,"E25.7");var subQ1=sQuery(id+"F0.wireOp",EDGE,"E25.1");var subQ2=sQuery(id+"F0.wireOp",EDGE,"E25.6");var subQ3=sQuery(id+"F0.wireOp",EDGE,"E25.5");var subQ4=sQuery(id+"F0.wireOp",EDGE,"E25.4");var subQ5=sQuery(id+"F0.wireOp",EDGE,"E25.0");var subQ6=sQuery(id+"F0.wireOp",EDGE,"E25.2");var subQ7=sQuery(id+"F0.wireOp",EDGE,"E25.3");Q4=makeQuery(id+"F8.boolean.opBoolean","INTERSECT",EDGE,{"derivedFrom":[makeQuery(id+"F5.boolean.opBoolean","SPLIT",FACE,{"disambiguationData":[TD([makeQuery(id+"F2.opExtrude","SWEPT_FACE",FACE,{"disambiguationData":[OSD([subQ5])]})])],"derivedFrom":makeQuery(id+"F3.boolean.opBoolean","COPY",FACE,{"derivedFrom":makeQuery(id+"F3.opExtrude","CAP_FACE",FACE,{"disambiguationData":[OSD([subQ5,subQ1,subQ6,subQ7,subQ4,subQ3,subQ2,subQ0])],"isStart":false})})}),makeQuery(id+"F8.opExtrude","SWEPT_FACE",FACE,{"disambiguationData":[OSD([sQuery(id+"F7.wireOp",EDGE,"E67")])]})]});}
            var Q5;
            Q5=makeQuery(id+"F8.boolean.opBoolean","INTERSECT",EDGE,{"disambiguationData":[OD(0.0)],"derivedFrom":[makeQuery(id+"F5.opExtrude","SWEPT_FACE",FACE,{"disambiguationData":[OSD([sQuery(id+"F4.wireOp",EDGE,"E30")])]}),makeQuery(id+"F8.opExtrude","SWEPT_FACE",FACE,{"disambiguationData":[OSD([sQuery(id+"F7.wireOp",EDGE,"E67")])]})]});
            fillet(context, id + "F14", {"entities" : qUnion([Q0, Q1, Q2, Q3, Q4, Q5]), "radius" : 3 * mm, "tangentPropagation" : true, "allowEdgeOverflow" : false});
        }
        {
            var Q0;
            Q0=makeQuery(id+"F1.opExtrude","CAP_EDGE",EDGE,{"disambiguationData":[OSD([sQuery(id+"F0.wireOp",EDGE,"E1.bottom")])],"isStart":false});
            fillet(context, id + "F15", {"entities" : qUnion([Q0]), "radius" : 2 * mm, "tangentPropagation" : true, "allowEdgeOverflow" : false});
        }
        {
            var Q0;
            {var subQ0=sQuery(id+"F0.wireOp",EDGE,"E22.filletArc");var subQ1=sQuery(id+"F0.wireOp",EDGE,"E7");var subQ2=sQuery(id+"F0.wireOp",EDGE,"E6");var subQ3=sQuery(id+"F0.wireOp",EDGE,"E5");var subQ4=sQuery(id+"F0.wireOp",EDGE,"E4");var subQ5=sQuery(id+"F0.wireOp",EDGE,"E1.bottom");var subQ6=sQuery(id+"F0.wireOp",EDGE,"E21.filletArc");var subQ7=sQuery(id+"F0.wireOp",EDGE,"E1.top");var subQ8=sQuery(id+"F0.wireOp",EDGE,"E1.left");var subQ9=sQuery(id+"F0.wireOp",EDGE,"E1.right");var subQ10=sQuery(id+"F0.wireOp",EDGE,"E23.filletArc");var subQ11=sQuery(id+"F0.wireOp",EDGE,"E24.filletArc");Q0=makeQuery(id+"F2.boolean.opBoolean","SPLIT",FACE,{"disambiguationData":[TD([makeQuery(id+"F1.opExtrude","SWEPT_FACE",FACE,{"disambiguationData":[OSD([subQ5])]})])],"derivedFrom":makeQuery(id+"F1.opExtrude","CAP_FACE",FACE,{"disambiguationData":[OSD([subQ5,subQ7,subQ8,subQ9,subQ4,subQ3,subQ2,subQ1,subQ6,subQ0,subQ10,subQ11])],"isStart":true})});}
            var sketch = newSketch(context, id + "F16", { "sketchPlane" : qUnion([Q0])});
            skLineSegment(sketch, "E79", {"start": v(0, 90) * mm, "end": v(0, 120) * mm});
            skCircle(sketch, "E80", {"center": v(0, 120) * mm, "radius": 6 * mm});
            skLineSegment(sketch, "E81", {"start": v(0, 120) * mm, "end": v(0, 108) * mm});
            skLineSegment(sketch, "E82", {"start": v(-33, 90) * mm, "end": v(-15, 108) * mm});
            skLineSegment(sketch, "E83", {"start": v(-15, 108) * mm, "end": v(-15, 120) * mm});
            skLineSegment(sketch, "E84", {"start": v(33, 90) * mm, "end": v(15, 108) * mm});
            skLineSegment(sketch, "E85", {"start": v(15, 108) * mm, "end": v(15, 120) * mm});
            skArc(sketch, "E86", {"start": v(15, 120) * mm, "mid": v(0, 135) * mm, "end": v(-15, 120) * mm});
            skLineSegment(sketch, "E87", {"start": v(-80, 0) * mm, "end": v(80, 0) * mm});
            skLineSegment(sketch, "E88.MirrorCS", {"start": v(-33, -90) * mm, "end": v(-15, -108) * mm});
            skLineSegment(sketch, "E89.MirrorCS", {"start": v(-15, -108) * mm, "end": v(-15, -120) * mm});
            skArc(sketch, "E90.MirrorCS", {"start": v(15, -120) * mm, "mid": v(0, -135) * mm, "end": v(-15, -120) * mm});
            skCircle(sketch, "E91.MirrorC", {"center": v(0, -120) * mm, "radius": 6 * mm});
            skLineSegment(sketch, "E92.MirrorCS", {"start": v(33, -90) * mm, "end": v(15, -108) * mm});
            skLineSegment(sketch, "E93.MirrorCS", {"start": v(15, -108) * mm, "end": v(15, -120) * mm});
            skLineSegment(sketch, "E94.MirrorCS", {"start": v(0, -90) * mm, "end": v(0, -120) * mm});
            skSolve(sketch);
        }
        {
            var Q0;
            {var subQ0=sQuery(id+"F16.wireOp",EDGE,"E88.MirrorCS");Q0=makeQuery(id+"F16.imprint","IMPRINT",FACE,{"disambiguationData":[TD([[makeQuery(id+"F16.imprint","IMPRINT",EDGE,{"derivedFrom":subQ0}),1.0]])]});}
            var Q1;
            Q1=makeQuery(id+"F16.imprint","IMPRINT",FACE,{"disambiguationData":[TD([[makeQuery(id+"F16.imprint","IMPRINT",EDGE,{"derivedFrom":makeQuery(id+"F1.opExtrude","CAP_EDGE",EDGE,{"disambiguationData":[OSD([sQuery(id+"F0.wireOp",EDGE,"E4")])],"isStart":true})}),-1.0]])]});
            var Q2;
            Q2=makeQuery(id+"F16.imprint","IMPRINT",FACE,{"disambiguationData":[TD([[makeQuery(id+"F16.imprint","IMPRINT",EDGE,{"derivedFrom":makeQuery(id+"F1.opExtrude","CAP_EDGE",EDGE,{"disambiguationData":[OSD([sQuery(id+"F0.wireOp",EDGE,"E6")])],"isStart":true})}),-1.0]])]});
            var Q3;
            Q3=makeQuery(id+"F16.imprint","IMPRINT",FACE,{"disambiguationData":[TD([[makeQuery(id+"F16.imprint","IMPRINT",EDGE,{"derivedFrom":sQuery(id+"F16.wireOp",EDGE,"E80")}),-1.0]])]});
            extrude(context, id + "F17", {"entities" : qUnion([Q0, Q1, Q2, Q3]), "operationType" : NewBodyOperationType.ADD, "depth" : 5 * mm});
        }
    });
